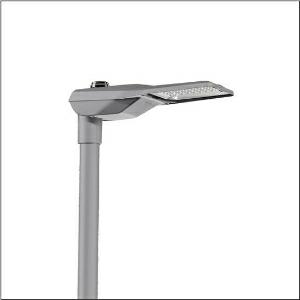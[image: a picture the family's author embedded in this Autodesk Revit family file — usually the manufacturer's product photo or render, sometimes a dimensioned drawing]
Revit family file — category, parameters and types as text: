
# Revit family: streetlight_sl_21_mini___st0_8a_5xe6c47n08hb_c463
name_source: partatom
category: Lighting Fixtures
units: mm (PartAtom-declared; Revit-internal decimal feet)

## family parameters
Cut with Voids When Loaded = No
Host = Face
Light Source = No
Part Type = Normal
Room Calculation Point = No
Round Connector Dimension = Use Diameter
Shared = No

## types (1)
- --- (1 x LED, 9430 lm, 66 W, 4000K)
    Apparent Load = 66 VA
    CIE Flux Codes = 38 75 97 100 100
    Color Rendering = 70
    Color Temperature = 4000K
    Default Elevation = 1800 mm
    Description = Streetlight SL 21 mini, mast luminaire, primary light control with lens, of PMMA, primary optical cover: cover, of toughened safety glass, transparent, light distribution: ST0.8a, light emission: direct distribution, primary light characteristic: asymmetric, installation type: side-entry, LED, 3G 1.5mm², High Power LED, rated luminous flux: 9.430lm, luminous efficacy: 143lm/W, light colour: 740, colour temperature: 4000K, control gear: NEMA (7pin), control: overheat protection, pre-setting: linear dimming characteristic, constant luminous flux control, time-dependent luminous flux control, flexible luminous flux parameterisation, mains connection: 230..240V, AC, 50/60Hz, connection cable pre-assembled, cable length: 8,5m, wiring characteristics: H07RN-F, start of lifetime: 66W, end of service life: 69W, reduction: 30W, luminaire housing, of diecast aluminium (EN AC-44300), powder-coated, Siteco® metallic grey (DB 702S), corrosivity category C5 mid according to DIN EN ISO 12944, multi-level sealing system, sealing non-destructively replaceable, inclination adjustable: 0°, 5°, 10°, 15°, length: 628mm, width: 235mm, height: 110mm, spigot size: 42mm (side-entry), mounting height: 4..8m, protection rating (complete): IP66, insulation class (complete): insulation class I (protective earthing), certification: CE, ENEC, ENEC+, VDE, impact resistance: IK10, permissible operating ambient temperature for outdoor applications: -40..+50°C, standard-compliant lighting for roads and squares, packaging unit: 1 piece

Light Distribution: ST0.8a
    Height = 110 mm
    Lamp = 1 x LED
    Lamp Light Flux = 9430 lm
    Lamp Power = 66 W
    Lamp count = 1
    Length = 625 mm
    Luminous efficacy = 143 lm/W
    Manufacturer = Siteco
    ModVariant = No
    Model = 5XE6C47N08HB
    Number of Poles = 1
    OnlyDefault = Yes
    Power Factor = 1
    Product Name = Streetlight SL 21 mini | ST0.8a
    Product group = mast luminaire | pylon top
    ProductGroupID = 6100
    Protection Class = Protection class I
    Protection Degree = IP 66
    RLX_Detail_Level = 1
    RLX_Emergency_Light_Flux = 0 lm
    RLX_Emergency_Type = 0
    RLX_Emergency_Type_DB = No
    RlxData = <blob elided: 26157 chars, md5=f861249c>
    Socket = socket
    Standby Power = 0 W
    System Light Flux = 9430 lm
    System Power = 66 W
    Type Comments = factory setting: luminous flux: 100 % | dim-lin: 254 | 670 mA
    Type Image = l_1294379.jpg
    URL = http://relux.com
    VarID = @adj_155627
    Voltage = 0 V
    Weight = 0.00 kg
    Width = 234 mm

## geometry (parser evidence)
native form markers: Blend x4, Sweep x10
no freeform markers — native parametric forms only
